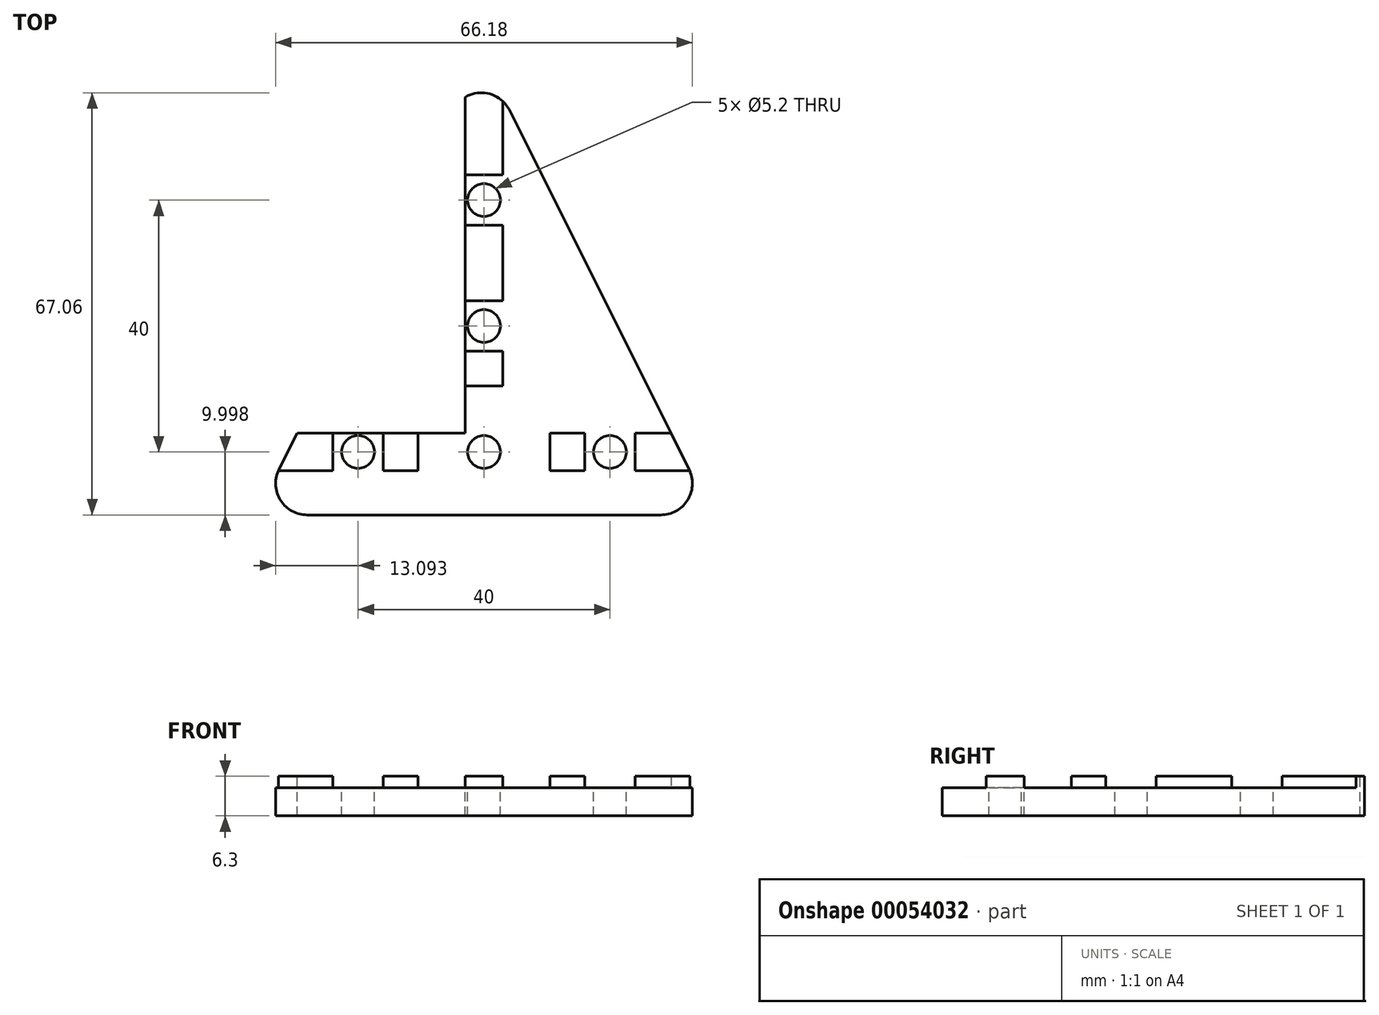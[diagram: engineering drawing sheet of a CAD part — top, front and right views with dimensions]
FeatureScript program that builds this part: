
annotation { "Feature Type Name" : "Feature", "Feature Type Description" : "" }
export const myFeature = defineFeature(function(context is Context, id is Id, definition is map)
    precondition{}
    {
        {
            var Q0;
            Q0=qCreatedBy(makeId("Top.planeOp"),FACE);
            var sketch = newSketch(context, id + "F0", { "sketchPlane" : qUnion([Q0])});
            skPoint(sketch, "E0", {"position": v(-19.32, 36.08) * mm});
            skPoint(sketch, "E1", {"position": v(-19.32, 16.08) * mm});
            skPoint(sketch, "E2", {"position": v(-19.32, -3.92) * mm});
            skPoint(sketch, "E3", {"position": v(0.68, -3.92) * mm});
            skPoint(sketch, "E4", {"position": v(-39.32, -3.92) * mm});
            skLineSegment(sketch, "E5", {"start": v(-55.5, -13.92) * mm, "end": v(-19.32, 58.44) * mm});
            skLineSegment(sketch, "E6", {"start": v(-55.5, -13.92) * mm, "end": v(16.86, -13.92) * mm});
            skLineSegment(sketch, "E7", {"start": v(16.86, -13.92) * mm, "end": v(-19.32, 58.44) * mm});
            skLineSegment(sketch, "E8", {"start": v(13.36, -6.92) * mm, "end": v(-52, -6.92) * mm});
            skLineSegment(sketch, "E9", {"start": v(-49, -0.92) * mm, "end": v(10.36, -0.92) * mm});
            skLineSegment(sketch, "E10", {"start": v(-22.32, -6.92) * mm, "end": v(-22.32, 52.44) * mm});
            skLineSegment(sketch, "E11", {"start": v(-16.32, -6.92) * mm, "end": v(-16.32, 52.44) * mm});
            skLineSegment(sketch, "E12", {"start": v(-22.32, 32.08) * mm, "end": v(-16.32, 32.08) * mm});
            skLineSegment(sketch, "E13", {"start": v(-16.32, 32.08) * mm, "end": v(-16.32, 20.08) * mm});
            skLineSegment(sketch, "E14", {"start": v(-16.32, 20.08) * mm, "end": v(-22.32, 20.08) * mm});
            skLineSegment(sketch, "E15", {"start": v(-22.32, 20.08) * mm, "end": v(-22.32, 12.08) * mm});
            skLineSegment(sketch, "E16", {"start": v(-22.32, 12.08) * mm, "end": v(-16.32, 12.08) * mm});
            skLineSegment(sketch, "E17", {"start": v(-22.32, 6.58) * mm, "end": v(-16.32, 6.58) * mm});
            skLineSegment(sketch, "E18", {"start": v(-29.82, -0.92) * mm, "end": v(-29.82, -6.92) * mm});
            skLineSegment(sketch, "E19", {"start": v(-35.32, -0.92) * mm, "end": v(-35.32, -6.92) * mm});
            skLineSegment(sketch, "E20", {"start": v(-8.82, -0.92) * mm, "end": v(-8.82, -6.92) * mm});
            skLineSegment(sketch, "E21", {"start": v(-3.32, -0.92) * mm, "end": v(-3.32, -6.92) * mm});
            skLineSegment(sketch, "E22", {"start": v(-22.32, 40.08) * mm, "end": v(-16.32, 40.08) * mm});
            skLineSegment(sketch, "E23", {"start": v(-43.32, -0.92) * mm, "end": v(-43.32, -6.92) * mm});
            skLineSegment(sketch, "E24", {"start": v(4.68, -0.92) * mm, "end": v(4.68, -6.92) * mm});
            skSolve(sketch);
        }
        {
            var Q0;
            Q0=makeQuery(id+"F0.imprint","IMPRINT",FACE,{"disambiguationData":[TD([[makeQuery(id+"F0.imprint","IMPRINT",EDGE,{"derivedFrom":sQuery(id+"F0.wireOp",EDGE,"E5")}),-1.0]])]});
            var Q1;
            {var subQ0=sQuery(id+"F0.wireOp",EDGE,"E9");var subQ1=sQuery(id+"F0.wireOp",EDGE,"E7");var subQ2=makeQuery(id+"F0.imprint","INTERSECT",VERTEX,{"derivedFrom":[subQ1,subQ0]});Q1=makeQuery(id+"F0.imprint","IMPRINT",FACE,{"disambiguationData":[TD([[makeQuery(id+"F0.imprint","IMPRINT",EDGE,{"disambiguationData":[TD([[subQ2,-1.0]])],"derivedFrom":subQ1}),1.0]])]});}
            var Q2;
            {var subQ4=sQuery(id+"F0.wireOp",EDGE,"E6");Q2=makeQuery(id+"F0.imprint","IMPRINT",FACE,{"disambiguationData":[TD([[makeQuery(id+"F0.imprint","IMPRINT",EDGE,{"derivedFrom":subQ4}),1.0]])]});}
            var Q3;
            {var subQ0=sQuery(id+"F0.wireOp",EDGE,"E8");var subQ1=sQuery(id+"F0.wireOp",EDGE,"E7");var subQ2=makeQuery(id+"F0.imprint","INTERSECT",VERTEX,{"derivedFrom":[subQ1,subQ0]});Q3=makeQuery(id+"F0.imprint","IMPRINT",FACE,{"disambiguationData":[TD([[makeQuery(id+"F0.imprint","IMPRINT",EDGE,{"disambiguationData":[TD([[subQ2,-1.0]])],"derivedFrom":subQ1}),1.0]])]});}
            var Q4;
            {var subQ0=sQuery(id+"F0.wireOp",EDGE,"E10");var subQ1=sQuery(id+"F0.wireOp",EDGE,"E8");var subQ2=makeQuery(id+"F0.imprint","INTERSECT",VERTEX,{"derivedFrom":[subQ1,subQ0]});Q4=makeQuery(id+"F0.imprint","IMPRINT",FACE,{"disambiguationData":[TD([[makeQuery(id+"F0.imprint","IMPRINT",EDGE,{"disambiguationData":[TD([[subQ2,1.0]])],"derivedFrom":subQ1}),-1.0]])]});}
            var Q5;
            {var subQ5=sQuery(id+"F0.wireOp",EDGE,"E7");var subQ6=sQuery(id+"F0.wireOp",EDGE,"E5");var subQ7=makeQuery(id+"F0.imprint","INTERSECT",VERTEX,{"derivedFrom":[subQ6,subQ5]});Q5=makeQuery(id+"F0.imprint","IMPRINT",FACE,{"disambiguationData":[TD([[makeQuery(id+"F0.imprint","IMPRINT",EDGE,{"disambiguationData":[TD([[subQ7,1.0]])],"derivedFrom":subQ6}),-1.0]])]});}
            var Q6;
            {var subQ0=sQuery(id+"F0.wireOp",EDGE,"E8");var subQ1=sQuery(id+"F0.wireOp",EDGE,"E5");var subQ2=makeQuery(id+"F0.imprint","INTERSECT",VERTEX,{"derivedFrom":[subQ1,subQ0]});Q6=makeQuery(id+"F0.imprint","IMPRINT",FACE,{"disambiguationData":[TD([[makeQuery(id+"F0.imprint","IMPRINT",EDGE,{"disambiguationData":[TD([[subQ2,-1.0]])],"derivedFrom":subQ1}),-1.0]])]});}
            var Q7;
            {var subQ3=sQuery(id+"F0.wireOp",EDGE,"E15");Q7=makeQuery(id+"F0.imprint","IMPRINT",FACE,{"disambiguationData":[TD([[makeQuery(id+"F0.imprint","IMPRINT",EDGE,{"derivedFrom":subQ3}),-1.0]])]});}
            var Q8;
            {var subQ0=sQuery(id+"F0.wireOp",EDGE,"E12");Q8=makeQuery(id+"F0.imprint","IMPRINT",FACE,{"disambiguationData":[TD([[makeQuery(id+"F0.imprint","IMPRINT",EDGE,{"derivedFrom":subQ0}),1.0]])]});}
            var Q9;
            {var subQ0=sQuery(id+"F0.wireOp",EDGE,"E12");Q9=makeQuery(id+"F0.imprint","IMPRINT",FACE,{"disambiguationData":[TD([[makeQuery(id+"F0.imprint","IMPRINT",EDGE,{"derivedFrom":subQ0}),-1.0]])]});}
            var Q10;
            {var subQ0=sQuery(id+"F0.wireOp",EDGE,"E14");Q10=makeQuery(id+"F0.imprint","IMPRINT",FACE,{"disambiguationData":[TD([[makeQuery(id+"F0.imprint","IMPRINT",EDGE,{"derivedFrom":subQ0}),1.0]])]});}
            var Q11;
            {var subQ0=sQuery(id+"F0.wireOp",EDGE,"E16");Q11=makeQuery(id+"F0.imprint","IMPRINT",FACE,{"disambiguationData":[TD([[makeQuery(id+"F0.imprint","IMPRINT",EDGE,{"derivedFrom":subQ0}),-1.0]])]});}
            var Q12;
            {var subQ5=sQuery(id+"F0.wireOp",EDGE,"E17");Q12=makeQuery(id+"F0.imprint","IMPRINT",FACE,{"disambiguationData":[TD([[makeQuery(id+"F0.imprint","IMPRINT",EDGE,{"derivedFrom":subQ5}),-1.0]])]});}
            var Q13;
            {var subQ3=sQuery(id+"F0.wireOp",EDGE,"E20");Q13=makeQuery(id+"F0.imprint","IMPRINT",FACE,{"disambiguationData":[TD([[makeQuery(id+"F0.imprint","IMPRINT",EDGE,{"derivedFrom":subQ3}),-1.0]])]});}
            var Q14;
            {var subQ0=sQuery(id+"F0.wireOp",EDGE,"E20");Q14=makeQuery(id+"F0.imprint","IMPRINT",FACE,{"disambiguationData":[TD([[makeQuery(id+"F0.imprint","IMPRINT",EDGE,{"derivedFrom":subQ0}),1.0]])]});}
            var Q15;
            {var subQ0=sQuery(id+"F0.wireOp",EDGE,"E21");Q15=makeQuery(id+"F0.imprint","IMPRINT",FACE,{"disambiguationData":[TD([[makeQuery(id+"F0.imprint","IMPRINT",EDGE,{"derivedFrom":subQ0}),1.0]])]});}
            var Q16;
            {var subQ3=sQuery(id+"F0.wireOp",EDGE,"E18");Q16=makeQuery(id+"F0.imprint","IMPRINT",FACE,{"disambiguationData":[TD([[makeQuery(id+"F0.imprint","IMPRINT",EDGE,{"derivedFrom":subQ3}),1.0]])]});}
            var Q17;
            {var subQ0=sQuery(id+"F0.wireOp",EDGE,"E18");Q17=makeQuery(id+"F0.imprint","IMPRINT",FACE,{"disambiguationData":[TD([[makeQuery(id+"F0.imprint","IMPRINT",EDGE,{"derivedFrom":subQ0}),-1.0]])]});}
            var Q18;
            {var subQ0=sQuery(id+"F0.wireOp",EDGE,"E19");Q18=makeQuery(id+"F0.imprint","IMPRINT",FACE,{"disambiguationData":[TD([[makeQuery(id+"F0.imprint","IMPRINT",EDGE,{"derivedFrom":subQ0}),-1.0]])]});}
            extrude(context, id + "F1", {"entities" : qUnion([Q0, Q1, Q2, Q3, Q4, Q5, Q6, Q7, Q8, Q9, Q10, Q11, Q12, Q13, Q14, Q15, Q16, Q17, Q18]), "oppositeDirection" : true, "depth" : 4.5 * mm});
        }
        {
            var Q0;
            {var subQ0=sQuery(id+"F0.wireOp",EDGE,"E12");Q0=makeQuery(id+"F0.imprint","IMPRINT",FACE,{"disambiguationData":[TD([[makeQuery(id+"F0.imprint","IMPRINT",EDGE,{"derivedFrom":subQ0}),-1.0]])]});}
            var Q1;
            {var subQ7=sQuery(id+"F0.wireOp",EDGE,"E22");Q1=makeQuery(id+"F0.imprint","IMPRINT",FACE,{"disambiguationData":[TD([[makeQuery(id+"F0.imprint","IMPRINT",EDGE,{"derivedFrom":subQ7}),1.0]])]});}
            var Q2;
            {var subQ0=sQuery(id+"F0.wireOp",EDGE,"E16");Q2=makeQuery(id+"F0.imprint","IMPRINT",FACE,{"disambiguationData":[TD([[makeQuery(id+"F0.imprint","IMPRINT",EDGE,{"derivedFrom":subQ0}),-1.0]])]});}
            var Q3;
            {var subQ0=sQuery(id+"F0.wireOp",EDGE,"E20");Q3=makeQuery(id+"F0.imprint","IMPRINT",FACE,{"disambiguationData":[TD([[makeQuery(id+"F0.imprint","IMPRINT",EDGE,{"derivedFrom":subQ0}),1.0]])]});}
            var Q4;
            {var subQ0=sQuery(id+"F0.wireOp",EDGE,"E18");Q4=makeQuery(id+"F0.imprint","IMPRINT",FACE,{"disambiguationData":[TD([[makeQuery(id+"F0.imprint","IMPRINT",EDGE,{"derivedFrom":subQ0}),-1.0]])]});}
            var Q5;
            {var subQ5=sQuery(id+"F0.wireOp",EDGE,"E23");Q5=makeQuery(id+"F0.imprint","IMPRINT",FACE,{"disambiguationData":[TD([[makeQuery(id+"F0.imprint","IMPRINT",EDGE,{"derivedFrom":subQ5}),-1.0]])]});}
            var Q6;
            {var subQ5=sQuery(id+"F0.wireOp",EDGE,"E24");Q6=makeQuery(id+"F0.imprint","IMPRINT",FACE,{"disambiguationData":[TD([[makeQuery(id+"F0.imprint","IMPRINT",EDGE,{"derivedFrom":subQ5}),1.0]])]});}
            extrude(context, id + "F2", {"entities" : qUnion([Q0, Q1, Q2, Q3, Q4, Q5, Q6]), "operationType" : NewBodyOperationType.ADD, "depth" : 1.8 * mm});
        }
        {
            var Q0;
            Q0=sQuery(id+"F0.wireOp",VERTEX,"E0");
            var Q1;
            Q1=sQuery(id+"F0.wireOp",VERTEX,"E1");
            var Q2;
            Q2=sQuery(id+"F0.wireOp",VERTEX,"E2");
            var Q3;
            Q3=sQuery(id+"F0.wireOp",VERTEX,"E3");
            var Q4;
            Q4=sQuery(id+"F0.wireOp",VERTEX,"E4");
            var Q5;
            Q5=makeQuery(id+"F1.opExtrude","SWEPT_BODY",BODY,{"disambiguationData":[OSD([sQuery(id+"F0.wireOp",EDGE,"E5"),sQuery(id+"F0.wireOp",EDGE,"E6"),sQuery(id+"F0.wireOp",EDGE,"E7")])]});
            hole(context, id + "F3", {"style" : HoleStyle.SIMPLE, "holeDiameter" : 5.2 * mm, "endStyle" : HoleEndStyle.THROUGH, "locations" : qUnion([Q0, Q1, Q2, Q3, Q4]), "scope" : qUnion([Q5])});
        }
        {
            var Q0;
            {var subQ0=sQuery(id+"F0.wireOp",EDGE,"E7");var subQ1=sQuery(id+"F0.wireOp",EDGE,"E5");Q0=makeQuery(id+"F2.boolean.opBoolean","MERGE",EDGE,{"derivedFrom":[makeQuery(id+"F1.opExtrude","SWEPT_EDGE",EDGE,{"disambiguationData":[OSD([subQ1,subQ0])]}),makeQuery(id+"F2.opExtrude","SWEPT_EDGE",EDGE,{"disambiguationData":[OSD([subQ1,subQ0])]})]});}
            var Q1;
            Q1=makeQuery(id+"F1.opExtrude","SWEPT_EDGE",EDGE,{"disambiguationData":[OSD([sQuery(id+"F0.wireOp",EDGE,"E5"),sQuery(id+"F0.wireOp",EDGE,"E6")])]});
            var Q2;
            Q2=makeQuery(id+"F1.opExtrude","SWEPT_EDGE",EDGE,{"disambiguationData":[OSD([sQuery(id+"F0.wireOp",EDGE,"E6"),sQuery(id+"F0.wireOp",EDGE,"E7")])]});
            fillet(context, id + "F4", {"entities" : qUnion([Q0, Q1, Q2]), "radius" : 5 * mm, "tangentPropagation" : true, "allowEdgeOverflow" : false});
        }
    });
